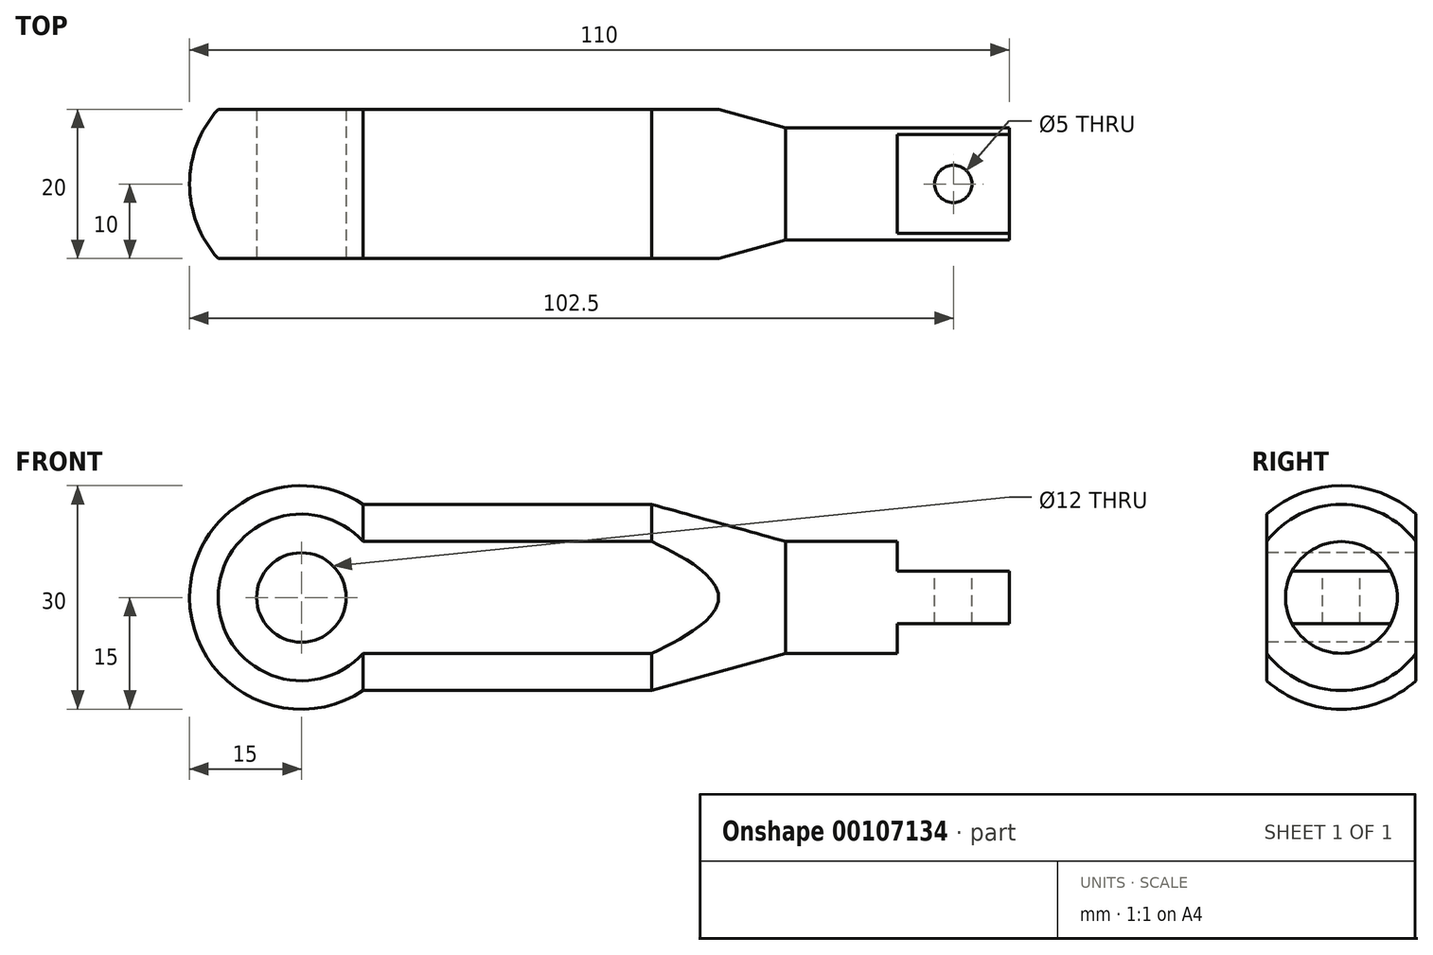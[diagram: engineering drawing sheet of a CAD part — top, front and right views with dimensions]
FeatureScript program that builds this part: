
annotation { "Feature Type Name" : "Feature", "Feature Type Description" : "" }
export const myFeature = defineFeature(function(context is Context, id is Id, definition is map)
    precondition{}
    {
        {
            var Q0;
            Q0=qCreatedBy(makeId("Front.planeOp"),FACE);
            var sketch = newSketch(context, id + "F0", { "sketchPlane" : qUnion([Q0])});
            skLineSegment(sketch, "E0", {"start": v(0, 0) * mm, "end": v(100.7, 0) * mm, "construction": true});
            skArc(sketch, "E1", {"start": v(8.3, -12.5) * mm, "mid": v(-7.1, -13.22) * mm, "end": v(-15, 0) * mm});
            skLineSegment(sketch, "E2", {"start": v(8.3, -12.5) * mm, "end": v(47, -12.5) * mm});
            skLineSegment(sketch, "E3", {"start": v(47, -12.5) * mm, "end": v(65, -7.5) * mm});
            skLineSegment(sketch, "E4", {"start": v(65, -7.5) * mm, "end": v(95, -7.5) * mm});
            skLineSegment(sketch, "E5", {"start": v(95, -7.5) * mm, "end": v(95, 0) * mm});
            skLineSegment(sketch, "E6", {"start": v(95, 0) * mm, "end": v(-15, 0) * mm});
            skSolve(sketch);
        }
        {
            var Q0;
            Q0 = qSketchRegion(id + "F0", true);
            var Q1;
            Q1=sQuery(id+"F0.wireOp",EDGE,"E0");
            revolve(context, id + "F1", {"entities" : qUnion([Q0]), "axis" : qUnion([Q1]), "revolveType" : RevolveType.FULL});
        }
        {
            var Q0;
            Q0=qCreatedBy(makeId("Front.planeOp"),FACE);
            var sketch = newSketch(context, id + "F2", { "sketchPlane" : qUnion([Q0])});
            skLineSegment(sketch, "E7.top", {"start": v(80, 3.5) * mm, "end": v(95, 3.5) * mm});
            skLineSegment(sketch, "E7.left", {"start": v(80, 7.5) * mm, "end": v(80, 3.5) * mm});
            skLineSegment(sketch, "E7.right", {"start": v(95, 7.5) * mm, "end": v(95, 3.5) * mm});
            skLineSegment(sketch, "E8", {"start": v(95, -7.5) * mm, "end": v(65, -7.5) * mm});
            skLineSegment(sketch, "E9", {"start": v(80, 7.5) * mm, "end": v(95, 7.5) * mm});
            skLineSegment(sketch, "E10", {"start": v(64.9, 0) * mm, "end": v(102.16, 0) * mm, "construction": true});
            skLineSegment(sketch, "E11.MirrorCS", {"start": v(95, -7.5) * mm, "end": v(95, -3.5) * mm});
            skLineSegment(sketch, "E12.MirrorCS", {"start": v(80, -3.5) * mm, "end": v(95, -3.5) * mm});
            skLineSegment(sketch, "E13.MirrorCS", {"start": v(80, -7.5) * mm, "end": v(95, -7.5) * mm});
            skLineSegment(sketch, "E14.MirrorCS", {"start": v(80, -7.5) * mm, "end": v(80, -3.5) * mm});
            skSolve(sketch);
        }
        {
            var Q0;
            Q0 = qSketchRegion(id + "F2", true);
            extrude(context, id + "F3", {"entities" : qUnion([Q0]), "operationType" : NewBodyOperationType.REMOVE, "endBound" : BoundingType.SYMMETRIC, "oppositeDirection" : true, "depth" : 25 * mm});
        }
        {
            var Q0;
            Q0=makeQuery(id+"F1.opRevolve","SWEPT_FACE",FACE,{"disambiguationData":[OSD([sQuery(id+"F0.wireOp",EDGE,"E5")])]});
            var sketch = newSketch(context, id + "F4", { "sketchPlane" : qUnion([Q0])});
            skLineSegment(sketch, "E15", {"start": v(-10, 11.18) * mm, "end": v(-10, -11.18) * mm});
            skArc(sketch, "E16", {"start": v(-10, 11.18) * mm, "mid": v(-15, 0) * mm, "end": v(-10, -11.18) * mm});
            skLineSegment(sketch, "E17", {"start": v(10, 11.18) * mm, "end": v(10, -11.18) * mm});
            skLineSegment(sketch, "E18", {"start": v(0, 27.7) * mm, "end": v(0, -24.74) * mm, "construction": true});
            skPoint(sketch, "E18.startSnap0", {"position": v(0, 3.5) * mm});
            skArc(sketch, "E19.trimOffspring", {"start": v(10, -11.18) * mm, "mid": v(15, 0) * mm, "end": v(10, 11.18) * mm});
            skSolve(sketch);
        }
        {
            var Q0;
            Q0 = qSketchRegion(id + "F4", true);
            extrude(context, id + "F5", {"entities" : qUnion([Q0]), "operationType" : NewBodyOperationType.REMOVE, "endBound" : BoundingType.THROUGH_ALL, "oppositeDirection" : true, "depth" : 25 * mm});
        }
        {
            var Q0;
            Q0=makeQuery(id+"F5.boolean.opBoolean","COPY",FACE,{"derivedFrom":makeQuery(id+"F5.opExtrude","SWEPT_FACE",FACE,{"disambiguationData":[OSD([sQuery(id+"F4.wireOp",EDGE,"E15")])]})});
            var sketch = newSketch(context, id + "F6", { "sketchPlane" : qUnion([Q0])});
            skCircle(sketch, "E20", {"center": v(0, 0) * mm, "radius": 6 * mm});
            skSolve(sketch);
        }
        {
            var Q0;
            Q0 = qSketchRegion(id + "F6", true);
            extrude(context, id + "F7", {"entities" : qUnion([Q0]), "operationType" : NewBodyOperationType.REMOVE, "endBound" : BoundingType.THROUGH_ALL, "oppositeDirection" : true, "depth" : 25 * mm});
        }
        {
            var Q0;
            Q0=makeQuery(id+"F3.boolean.opBoolean","COPY",FACE,{"derivedFrom":makeQuery(id+"F3.opExtrude","SWEPT_FACE",FACE,{"disambiguationData":[OSD([sQuery(id+"F2.wireOp",EDGE,"E7.top")])]})});
            var sketch = newSketch(context, id + "F8", { "sketchPlane" : qUnion([Q0])});
            skCircle(sketch, "E21", {"center": v(87.5, 0) * mm, "radius": 2.5 * mm});
            skSolve(sketch);
        }
        {
            var Q0;
            Q0 = qSketchRegion(id + "F8", true);
            extrude(context, id + "F9", {"entities" : qUnion([Q0]), "operationType" : NewBodyOperationType.REMOVE, "endBound" : BoundingType.THROUGH_ALL, "oppositeDirection" : true, "depth" : 25 * mm});
        }
    });
